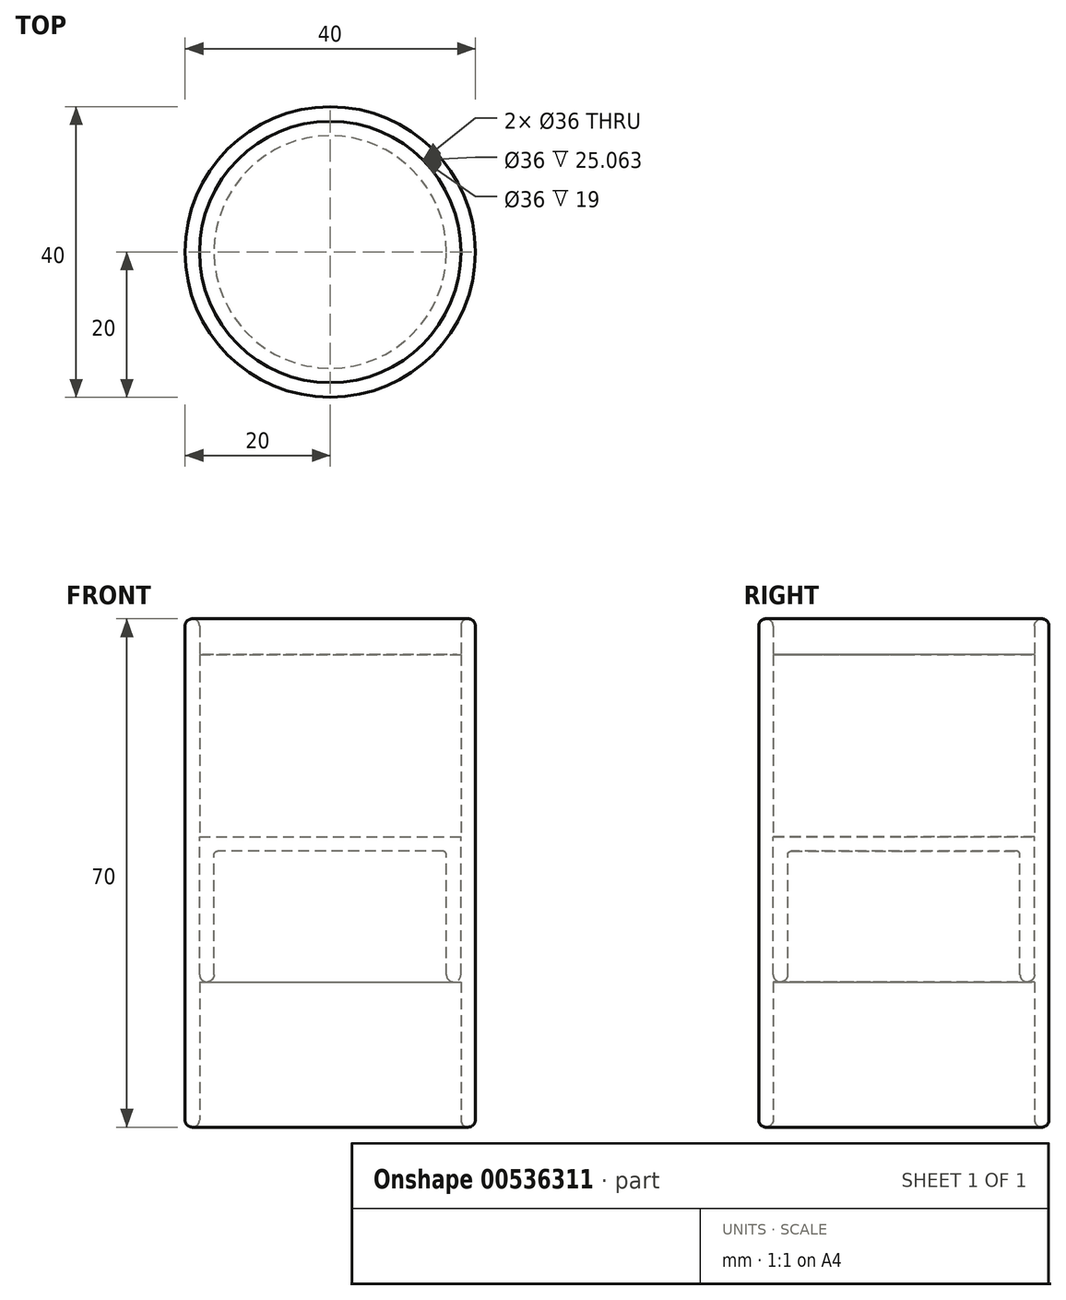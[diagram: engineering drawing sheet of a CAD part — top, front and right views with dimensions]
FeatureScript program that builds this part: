
annotation { "Feature Type Name" : "Feature", "Feature Type Description" : "" }
export const myFeature = defineFeature(function(context is Context, id is Id, definition is map)
    precondition{}
    {
        {
            var Q0;
            Q0=qCreatedBy(makeId("Front.planeOp"),FACE);
            var sketch = newSketch(context, id + "F0", { "sketchPlane" : qUnion([Q0])});
            skLineSegment(sketch, "E0", {"start": v(0, 0) * mm, "end": v(0, 70) * mm});
            skLineSegment(sketch, "E1", {"start": v(0, 70) * mm, "end": v(2, 70) * mm});
            skLineSegment(sketch, "E2", {"start": v(2, 70) * mm, "end": v(2, 65.06) * mm});
            skLineSegment(sketch, "E3", {"start": v(0, 0) * mm, "end": v(2, 0) * mm});
            skLineSegment(sketch, "E4", {"start": v(2, 0) * mm, "end": v(2, 20) * mm});
            skLineSegment(sketch, "E5", {"start": v(0, 35) * mm, "end": v(20, 35) * mm, "construction": true});
            skLineSegment(sketch, "E6", {"start": v(20, 47.4) * mm, "end": v(20, 26.2) * mm, "construction": true});
            skSolve(sketch);
        }
        {
            var Q0;
            Q0=sQuery(id+"F0.wireOp",EDGE,"E6");
            var Q1;
            Q1=sQuery(id+"F0.wireOp",EDGE,"E2");
            var Q2;
            Q2=sQuery(id+"F0.wireOp",EDGE,"E1");
            var Q3;
            Q3=sQuery(id+"F0.wireOp",EDGE,"E0");
            var Q4;
            Q4=sQuery(id+"F0.wireOp",EDGE,"E3");
            var Q5;
            Q5=sQuery(id+"F0.wireOp",EDGE,"E4");
            var Q6;
            Q6=qConstructionFilter(qBodyType(qCreatedBy(id+"F2",EDGE),BodyType.WIRE),ConstructionObject.NO);
            var Q7;
            Q7=sQuery(id+"F0.wireOp",EDGE,"E6");
            revolve(context, id + "F1", {"bodyType" : ToolBodyType.SURFACE, "surfaceEntities" : qUnion([Q0, Q1, Q2, Q3, Q4, Q5, Q6]), "axis" : qUnion([Q7]), "revolveType" : RevolveType.FULL});
        }
        {
            var Q0;
            Q0=qCreatedBy(makeId("Front.planeOp"),FACE);
            var sketch = newSketch(context, id + "F2", { "sketchPlane" : qUnion([Q0])});
            skLineSegment(sketch, "E7.0", {"start": v(2, 20) * mm, "end": v(38, 20) * mm});
            skLineSegment(sketch, "E8", {"start": v(2, 20) * mm, "end": v(2, 40) * mm});
            skLineSegment(sketch, "E9", {"start": v(20, 20) * mm, "end": v(20, 40) * mm});
            skLineSegment(sketch, "E10", {"start": v(20, 40) * mm, "end": v(2, 40) * mm});
            skLineSegment(sketch, "E11.0", {"start": v(20, 38) * mm, "end": v(4, 38) * mm});
            skLineSegment(sketch, "E11.1", {"start": v(4, 20) * mm, "end": v(4, 38) * mm});
            skLineSegment(sketch, "E12", {"start": v(4, 20) * mm, "end": v(2, 20) * mm});
            skSolve(sketch);
        }
        {
            var Q0;
            Q0=qSketchRegion(id+"F2",true);
            var Q1;
            Q1=sQuery(id+"F2.wireOp",EDGE,"E8");
            var Q2;
            Q2=sQuery(id+"F2.wireOp",EDGE,"E11.1");
            var Q3;
            Q3=sQuery(id+"F2.wireOp",EDGE,"E11.0");
            var Q4;
            Q4=sQuery(id+"F2.wireOp",EDGE,"E10");
            var Q5;
            Q5=sQuery(id+"F2.wireOp",EDGE,"E12");
            var Q6;
            Q6=sQuery(id+"F2.wireOp",EDGE,"E9");
            revolve(context, id + "F3", {"bodyType" : ToolBodyType.SURFACE, "entities" : qUnion([Q0]), "surfaceEntities" : qUnion([Q1, Q2, Q3, Q4, Q5]), "axis" : qUnion([Q6]), "revolveType" : RevolveType.FULL});
        }
        {
            var Q0;
            Q0=qCreatedBy(makeId("Front.planeOp"),FACE);
            var sketch = newSketch(context, id + "F4", { "sketchPlane" : qUnion([Q0])});
            skLineSegment(sketch, "E13.0", {"start": v(2, 40) * mm, "end": v(20, 40) * mm});
            skLineSegment(sketch, "E14", {"start": v(2, 65.06) * mm, "end": v(2, 40) * mm});
            skLineSegment(sketch, "E15", {"start": v(20, 65.06) * mm, "end": v(20, 40) * mm});
            skPoint(sketch, "E16.orphan", {"position": v(38, 65.06) * mm});
            skPoint(sketch, "E17.orphan", {"position": v(38, 40) * mm});
            skSolve(sketch);
        }
        {
            var Q0;
            Q0=qSketchRegion(id+"F4",true);
            var Q1;
            Q1=sQuery(id+"F4.wireOp",EDGE,"E14");
            var Q2;
            Q2=sQuery(id+"F4.wireOp",EDGE,"E13.0");
            var Q3;
            Q3=sQuery(id+"F4.wireOp",EDGE,"E15");
            revolve(context, id + "F5", {"bodyType" : ToolBodyType.SURFACE, "entities" : qUnion([Q0]), "surfaceEntities" : qUnion([Q1, Q2]), "axis" : qUnion([Q3]), "revolveType" : RevolveType.FULL});
        }
        {
            var Q0;
            Q0=qCreatedBy(makeId("Front.planeOp"),FACE);
            var sketch = newSketch(context, id + "F6", { "sketchPlane" : qUnion([Q0])});
            skLineSegment(sketch, "E18.0", {"start": v(20, 65.06) * mm, "end": v(2, 65.06) * mm});
            skLineSegment(sketch, "E19", {"start": v(20, 65.06) * mm, "end": v(20, 54.77) * mm});
            skPoint(sketch, "E20.orphan", {"position": v(38, 65.06) * mm});
            skSolve(sketch);
        }
        {
            var Q0;
            Q0=qSketchRegion(id+"F6",true);
            var Q1;
            Q1=sQuery(id+"F6.wireOp",EDGE,"E18.0");
            var Q2;
            Q2=sQuery(id+"F6.wireOp",EDGE,"E19");
            revolve(context, id + "F7", {"bodyType" : ToolBodyType.SURFACE, "entities" : qUnion([Q0]), "surfaceEntities" : qUnion([Q1]), "axis" : qUnion([Q2]), "revolveType" : RevolveType.FULL});
        }
        {
            var Q0;
            Q0=makeQuery(id+"F3.opRevolve","SWEPT_FACE",FACE,{"disambiguationData":[OSD([sQuery(id+"F2.wireOp",EDGE,"E12")])]});
            fillet(context, id + "F8", {"entities" : qUnion([Q0]), "radius" : 1 * mm, "tangentPropagation" : true, "allowEdgeOverflow" : false});
        }
        {
            var Q0;
            Q0=makeQuery(id+"F3.opRevolve","SWEPT_EDGE",EDGE,{"disambiguationData":[OSD([sQuery(id+"F2.wireOp",VERTEX,"E11.0.end")])]});
            fillet(context, id + "F9", {"entities" : qUnion([Q0]), "radius" : 0.5 * mm, "tangentPropagation" : true, "allowEdgeOverflow" : false});
        }
        {
            var Q0;
            Q0=makeQuery(id+"F1.opRevolve","SWEPT_FACE",FACE,{"disambiguationData":[OSD([sQuery(id+"F0.wireOp",EDGE,"E1")])]});
            var Q1;
            Q1=makeQuery(id+"F1.opRevolve","SWEPT_FACE",FACE,{"disambiguationData":[OSD([sQuery(id+"F0.wireOp",EDGE,"E3")])]});
            fillet(context, id + "F10", {"entities" : qUnion([Q0, Q1]), "radius" : 1 * mm, "tangentPropagation" : true, "allowEdgeOverflow" : false});
        }
    });
